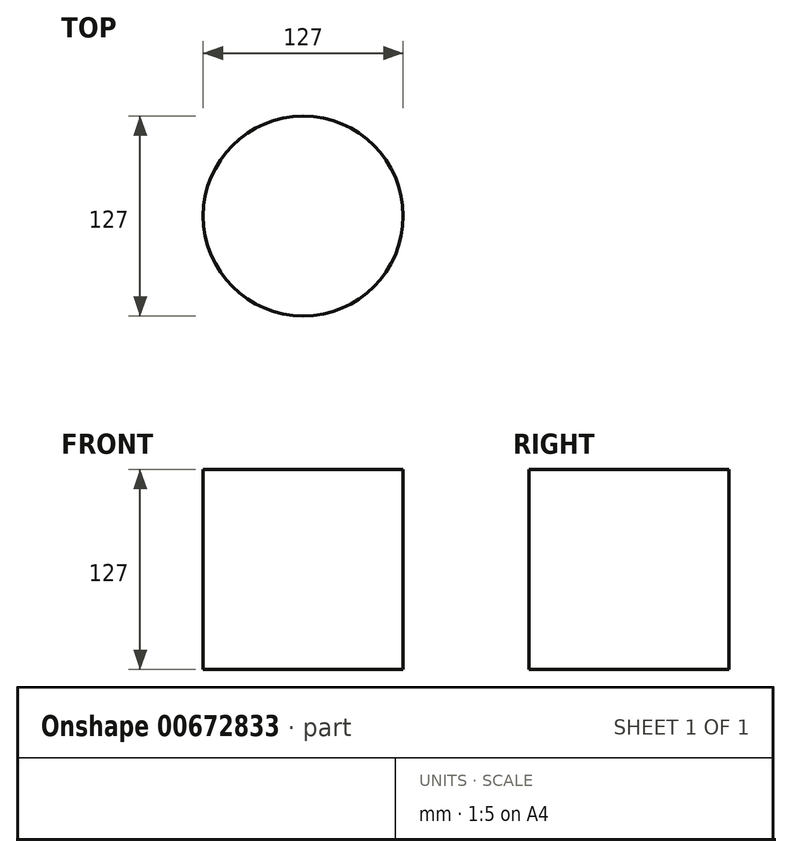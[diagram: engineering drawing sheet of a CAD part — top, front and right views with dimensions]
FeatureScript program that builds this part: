
annotation { "Feature Type Name" : "Feature", "Feature Type Description" : "" }
export const myFeature = defineFeature(function(context is Context, id is Id, definition is map)
    precondition{}
    {
        {
            var Q0;
            Q0=qCreatedBy(makeId("Top.planeOp"),FACE);
            var sketch = newSketch(context, id + "F0", { "sketchPlane" : qUnion([Q0])});
            skCircle(sketch, "E0", {"center": v(0, 0) * mm, "radius": 63.5 * mm});
            skSolve(sketch);
        }
        {
            var Q0;
            Q0 = qSketchRegion(id + "F0", true);
            extrude(context, id + "F1", {"entities" : qUnion([Q0]), "depth" : 127 * mm, "offsetDistance" : 25.4 * mm});
        }
    });
